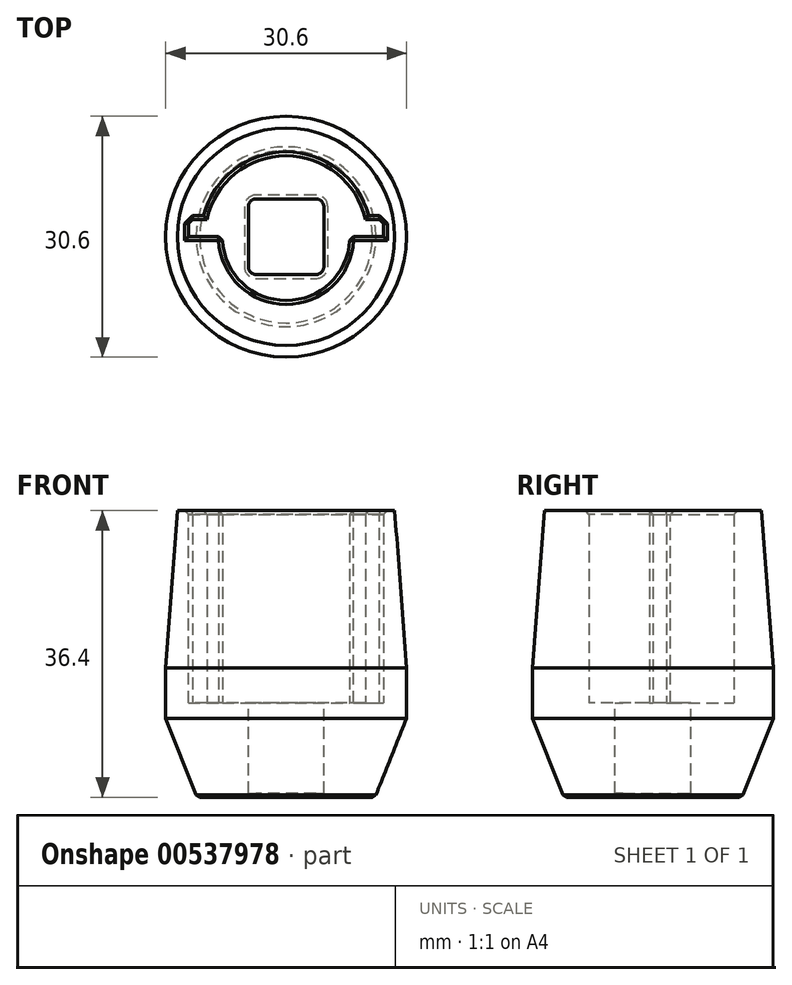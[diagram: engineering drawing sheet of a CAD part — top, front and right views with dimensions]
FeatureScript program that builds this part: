
annotation { "Feature Type Name" : "Feature", "Feature Type Description" : "" }
export const myFeature = defineFeature(function(context is Context, id is Id, definition is map)
    precondition{}
    {
        {
            var Q0;
            Q0=qCreatedBy(makeId("Top.planeOp"),FACE);
            var sketch = newSketch(context, id + "F0", { "sketchPlane" : qUnion([Q0])});
            skCircle(sketch, "E0", {"center": v(0, 0) * mm, "radius": 10.3 * mm});
            skCircle(sketch, "E1", {"center": v(0, 0) * mm, "radius": 15.3 * mm});
            skLineSegment(sketch, "E2", {"start": v(-15.3, 0) * mm, "end": v(15.3, 0) * mm});
            skCircle(sketch, "E3", {"center": v(0, 0) * mm, "radius": 8.1 * mm});
            skLineSegment(sketch, "E4.bottom", {"start": v(4.8, 4.8) * mm, "end": v(-4.8, 4.8) * mm});
            skLineSegment(sketch, "E4.top", {"start": v(4.8, -4.8) * mm, "end": v(-4.8, -4.8) * mm});
            skLineSegment(sketch, "E4.left", {"start": v(4.8, 4.8) * mm, "end": v(4.8, -4.8) * mm});
            skLineSegment(sketch, "E4.right", {"start": v(-4.8, 4.8) * mm, "end": v(-4.8, -4.8) * mm});
            skLineSegment(sketch, "E5", {"start": v(-10.06, 2.2) * mm, "end": v(-12.4, 2.2) * mm});
            skLineSegment(sketch, "E6", {"start": v(-12.4, 2.2) * mm, "end": v(-12.4, -2.2) * mm});
            skLineSegment(sketch, "E7", {"start": v(-12.4, -2.2) * mm, "end": v(-10.06, -2.2) * mm});
            skLineSegment(sketch, "E8.MirrorCS", {"start": v(10.06, 2.2) * mm, "end": v(12.4, 2.2) * mm});
            skLineSegment(sketch, "E9.MirrorCS", {"start": v(12.4, 2.2) * mm, "end": v(12.4, -2.2) * mm});
            skLineSegment(sketch, "E10.MirrorCS", {"start": v(12.4, -2.2) * mm, "end": v(10.06, -2.2) * mm});
            skSolve(sketch);
        }
        {
            var Q0;
            {var subQ5=sQuery(id+"F0.wireOp",EDGE,"E7");Q0=makeQuery(id+"F0.imprint","IMPRINT",FACE,{"disambiguationData":[TD([[makeQuery(id+"F0.imprint","IMPRINT",EDGE,{"derivedFrom":subQ5}),-1.0]])]});}
            var Q1;
            {var subQ9=sQuery(id+"F0.wireOp",EDGE,"E5");Q1=makeQuery(id+"F0.imprint","IMPRINT",FACE,{"disambiguationData":[TD([[makeQuery(id+"F0.imprint","IMPRINT",EDGE,{"derivedFrom":subQ9}),-1.0]])]});}
            extrude(context, id + "F1", {"entities" : qUnion([Q0, Q1]), "depth" : 24.4 * mm, "offsetDistance" : 25 * mm});
        }
        {
            var Q0;
            {var subQ0=sQuery(id+"F0.wireOp",EDGE,"E4.bottom");Q0=makeQuery(id+"F0.imprint","IMPRINT",FACE,{"disambiguationData":[TD([[makeQuery(id+"F0.imprint","IMPRINT",EDGE,{"derivedFrom":subQ0}),-1.0]])]});}
            var Q1;
            {var subQ0=sQuery(id+"F0.wireOp",EDGE,"E0");var subQ4=makeQuery(id+"F0.imprint","INTERSECT",VERTEX,{"derivedFrom":[subQ0,sQuery(id+"F0.wireOp",EDGE,"E8.MirrorCS")]});Q1=makeQuery(id+"F0.imprint","IMPRINT",FACE,{"disambiguationData":[TD([[makeQuery(id+"F0.imprint","IMPRINT",EDGE,{"disambiguationData":[TD([[subQ4,1.0]])],"derivedFrom":subQ0}),1.0]])]});}
            var Q2;
            {var subQ9=sQuery(id+"F0.wireOp",EDGE,"E5");Q2=makeQuery(id+"F0.imprint","IMPRINT",FACE,{"disambiguationData":[TD([[makeQuery(id+"F0.imprint","IMPRINT",EDGE,{"derivedFrom":subQ9}),-1.0]])]});}
            var Q3;
            {var subQ0=sQuery(id+"F0.wireOp",EDGE,"E4.top");Q3=makeQuery(id+"F0.imprint","IMPRINT",FACE,{"disambiguationData":[TD([[makeQuery(id+"F0.imprint","IMPRINT",EDGE,{"derivedFrom":subQ0}),1.0]])]});}
            var Q4;
            {var subQ1=sQuery(id+"F0.wireOp",EDGE,"E0");var subQ7=makeQuery(id+"F0.imprint","INTERSECT",VERTEX,{"derivedFrom":[subQ1,sQuery(id+"F0.wireOp",EDGE,"E7")]});Q4=makeQuery(id+"F0.imprint","IMPRINT",FACE,{"disambiguationData":[TD([[makeQuery(id+"F0.imprint","IMPRINT",EDGE,{"disambiguationData":[TD([[subQ7,1.0]])],"derivedFrom":subQ1}),1.0]])]});}
            var Q5;
            {var subQ5=sQuery(id+"F0.wireOp",EDGE,"E7");Q5=makeQuery(id+"F0.imprint","IMPRINT",FACE,{"disambiguationData":[TD([[makeQuery(id+"F0.imprint","IMPRINT",EDGE,{"derivedFrom":subQ5}),-1.0]])]});}
            var Q6;
            {var subQ0=sQuery(id+"F0.wireOp",EDGE,"E10.MirrorCS");Q6=makeQuery(id+"F0.imprint","IMPRINT",FACE,{"disambiguationData":[TD([[makeQuery(id+"F0.imprint","IMPRINT",EDGE,{"derivedFrom":subQ0}),-1.0]])]});}
            var Q7;
            {var subQ0=sQuery(id+"F0.wireOp",EDGE,"E8.MirrorCS");Q7=makeQuery(id+"F0.imprint","IMPRINT",FACE,{"disambiguationData":[TD([[makeQuery(id+"F0.imprint","IMPRINT",EDGE,{"derivedFrom":subQ0}),-1.0]])]});}
            var Q8;
            {var subQ0=sQuery(id+"F0.wireOp",EDGE,"E7");Q8=makeQuery(id+"F0.imprint","IMPRINT",FACE,{"disambiguationData":[TD([[makeQuery(id+"F0.imprint","IMPRINT",EDGE,{"derivedFrom":subQ0}),1.0]])]});}
            var Q9;
            {var subQ0=sQuery(id+"F0.wireOp",EDGE,"E5");Q9=makeQuery(id+"F0.imprint","IMPRINT",FACE,{"disambiguationData":[TD([[makeQuery(id+"F0.imprint","IMPRINT",EDGE,{"derivedFrom":subQ0}),1.0]])]});}
            extrude(context, id + "F2", {"entities" : qUnion([Q0, Q1, Q2, Q3, Q4, Q5, Q6, Q7, Q8, Q9]), "operationType" : NewBodyOperationType.ADD, "oppositeDirection" : true, "depth" : 12 * mm, "offsetDistance" : 25 * mm});
        }
        {
            var Q0;
            Q0=makeQuery(id+"F2.opExtrude","SWEPT_EDGE",EDGE,{"disambiguationData":[OSD([sQuery(id+"F0.wireOp",EDGE,"E4.bottom"),sQuery(id+"F0.wireOp",EDGE,"E4.right")])]});
            var Q1;
            Q1=makeQuery(id+"F2.opExtrude","SWEPT_EDGE",EDGE,{"disambiguationData":[OSD([sQuery(id+"F0.wireOp",EDGE,"E4.bottom"),sQuery(id+"F0.wireOp",EDGE,"E4.left")])]});
            var Q2;
            Q2=makeQuery(id+"F2.opExtrude","SWEPT_EDGE",EDGE,{"disambiguationData":[OSD([sQuery(id+"F0.wireOp",EDGE,"E4.top"),sQuery(id+"F0.wireOp",EDGE,"E4.left")])]});
            var Q3;
            Q3=makeQuery(id+"F2.opExtrude","SWEPT_EDGE",EDGE,{"disambiguationData":[OSD([sQuery(id+"F0.wireOp",EDGE,"E4.top"),sQuery(id+"F0.wireOp",EDGE,"E4.right")])]});
            fillet(context, id + "F3", {"entities" : qUnion([Q0, Q1, Q2, Q3]), "radius" : 1 * mm, "tangentPropagation" : true, "allowEdgeOverflow" : false});
        }
        {
            var Q0;
            {var subQ0=sQuery(id+"F0.wireOp",EDGE,"E10.MirrorCS");Q0=makeQuery(id+"F0.imprint","IMPRINT",FACE,{"disambiguationData":[TD([[makeQuery(id+"F0.imprint","IMPRINT",EDGE,{"derivedFrom":subQ0}),-1.0]])]});}
            var Q1;
            {var subQ1=sQuery(id+"F0.wireOp",EDGE,"E0");var subQ7=makeQuery(id+"F0.imprint","INTERSECT",VERTEX,{"derivedFrom":[subQ1,sQuery(id+"F0.wireOp",EDGE,"E7")]});Q1=makeQuery(id+"F0.imprint","IMPRINT",FACE,{"disambiguationData":[TD([[makeQuery(id+"F0.imprint","IMPRINT",EDGE,{"disambiguationData":[TD([[subQ7,1.0]])],"derivedFrom":subQ1}),1.0]])]});}
            var Q2;
            {var subQ0=sQuery(id+"F0.wireOp",EDGE,"E7");Q2=makeQuery(id+"F0.imprint","IMPRINT",FACE,{"disambiguationData":[TD([[makeQuery(id+"F0.imprint","IMPRINT",EDGE,{"derivedFrom":subQ0}),1.0]])]});}
            var Q3;
            Q3=makeQuery(id+"F1.opExtrude","CAP_FACE",FACE,{"disambiguationData":[OSD([sQuery(id+"F0.wireOp",EDGE,"E0"),sQuery(id+"F0.wireOp",EDGE,"E1"),sQuery(id+"F0.wireOp",EDGE,"E5"),sQuery(id+"F0.wireOp",EDGE,"E6"),sQuery(id+"F0.wireOp",EDGE,"E7"),sQuery(id+"F0.wireOp",EDGE,"E8.MirrorCS"),sQuery(id+"F0.wireOp",EDGE,"E9.MirrorCS"),sQuery(id+"F0.wireOp",EDGE,"E10.MirrorCS")])],"isStart":false});
            extrude(context, id + "F4", {"entities" : qUnion([Q0, Q1, Q2]), "operationType" : NewBodyOperationType.ADD, "endBound" : BoundingType.UP_TO_SURFACE, "depth" : 25 * mm, "endBoundEntityFace" : qUnion([Q3]), "offsetDistance" : 25 * mm});
        }
        {
            var Q0;
            Q0=makeQuery(id+"F2.opExtrude","CAP_EDGE",EDGE,{"disambiguationData":[OSD([sQuery(id+"F0.wireOp",EDGE,"E1")])],"isStart":false});
            chamfer(context, id + "F5", {"entities" : qUnion([Q0]), "chamferType" : ChamferType.TWO_OFFSETS, "width1" : 10 * mm, "oppositeDirection" : false, "width2" : 4 * mm, "tangentPropagation" : true});
        }
        {
            var Q0;
            Q0=makeQuery(id+"F1.opExtrude","CAP_EDGE",EDGE,{"disambiguationData":[OSD([sQuery(id+"F0.wireOp",EDGE,"E1")])],"isStart":false});
            chamfer(context, id + "F6", {"entities" : qUnion([Q0]), "chamferType" : ChamferType.TWO_OFFSETS, "width1" : 20 * mm, "oppositeDirection" : true, "width2" : 1.5 * mm, "tangentPropagation" : true});
        }
        {
            var Q0;
            Q0=makeQuery(id+"F2.opExtrude","CAP_FACE",FACE,{"disambiguationData":[OSD([sQuery(id+"F0.wireOp",EDGE,"E1"),sQuery(id+"F0.wireOp",EDGE,"E4.bottom"),sQuery(id+"F0.wireOp",EDGE,"E4.top"),sQuery(id+"F0.wireOp",EDGE,"E4.left"),sQuery(id+"F0.wireOp",EDGE,"E4.right")])],"isStart":false});
            var Q1;
            Q1=makeQuery(id+"F1.opExtrude","SWEPT_EDGE",EDGE,{"disambiguationData":[OSD([sQuery(id+"F0.wireOp",EDGE,"E8.MirrorCS"),sQuery(id+"F0.wireOp",EDGE,"E9.MirrorCS")])]});
            var Q2;
            Q2=makeQuery(id+"F1.opExtrude","SWEPT_EDGE",EDGE,{"disambiguationData":[OSD([sQuery(id+"F0.wireOp",EDGE,"E9.MirrorCS"),sQuery(id+"F0.wireOp",EDGE,"E10.MirrorCS")])]});
            var Q3;
            Q3=makeQuery(id+"F1.opExtrude","SWEPT_EDGE",EDGE,{"disambiguationData":[OSD([sQuery(id+"F0.wireOp",EDGE,"E5"),sQuery(id+"F0.wireOp",EDGE,"E6")])]});
            var Q4;
            Q4=makeQuery(id+"F1.opExtrude","SWEPT_EDGE",EDGE,{"disambiguationData":[OSD([sQuery(id+"F0.wireOp",EDGE,"E6"),sQuery(id+"F0.wireOp",EDGE,"E7")])]});
            var Q5;
            Q5=makeQuery(id+"F1.opExtrude","CAP_EDGE",EDGE,{"disambiguationData":[OSD([sQuery(id+"F0.wireOp",EDGE,"E7")])],"isStart":false});
            var Q6;
            Q6=makeQuery(id+"F1.opExtrude","CAP_EDGE",EDGE,{"disambiguationData":[OSD([sQuery(id+"F0.wireOp",EDGE,"E10.MirrorCS")])],"isStart":false});
            var Q7;
            {var subQ0=sQuery(id+"F0.wireOp",EDGE,"E0");Q7=makeQuery(id+"F1.opExtrude","CAP_EDGE",EDGE,{"disambiguationData":[OSD([subQ0]),TDD([makeQuery(id+"F0.imprint","IMPRINT",EDGE,{"disambiguationData":[TD([[makeQuery(id+"F0.imprint","INTERSECT",VERTEX,{"derivedFrom":[subQ0,sQuery(id+"F0.wireOp",EDGE,"E5")]}),1.0]])],"derivedFrom":subQ0})])],"isStart":true});}
            var Q8;
            {var subQ0=sQuery(id+"F0.wireOp",EDGE,"E0");Q8=makeQuery(id+"F1.opExtrude","CAP_EDGE",EDGE,{"disambiguationData":[OSD([subQ0]),TDD([makeQuery(id+"F0.imprint","IMPRINT",EDGE,{"disambiguationData":[TD([[makeQuery(id+"F0.imprint","INTERSECT",VERTEX,{"derivedFrom":[subQ0,sQuery(id+"F0.wireOp",EDGE,"E7")]}),-1.0]])],"derivedFrom":subQ0})])],"isStart":true});}
            var Q9;
            {var subQ0=sQuery(id+"F0.wireOp",EDGE,"E0");Q9=makeQuery(id+"F1.opExtrude","CAP_EDGE",EDGE,{"disambiguationData":[OSD([subQ0]),TDD([makeQuery(id+"F0.imprint","IMPRINT",EDGE,{"disambiguationData":[TD([[makeQuery(id+"F0.imprint","INTERSECT",VERTEX,{"derivedFrom":[subQ0,sQuery(id+"F0.wireOp",EDGE,"E5")]}),1.0]])],"derivedFrom":subQ0})])],"isStart":false});}
            var Q10;
            {var subQ0=sQuery(id+"F0.wireOp",EDGE,"E0");Q10=makeQuery(id+"F1.opExtrude","CAP_EDGE",EDGE,{"disambiguationData":[OSD([subQ0]),TDD([makeQuery(id+"F0.imprint","IMPRINT",EDGE,{"disambiguationData":[TD([[makeQuery(id+"F0.imprint","INTERSECT",VERTEX,{"derivedFrom":[subQ0,sQuery(id+"F0.wireOp",EDGE,"E7")]}),-1.0]])],"derivedFrom":subQ0})])],"isStart":false});}
            var Q11;
            {var subQ0=sQuery(id+"F0.wireOp",EDGE,"E3");var subQ1=sQuery(id+"F0.wireOp",EDGE,"E2");Q11=makeQuery(id+"F4.opExtrude","SWEPT_EDGE",EDGE,{"disambiguationData":[OSD([subQ1,subQ0]),TDD([makeQuery(id+"F0.imprint","INTERSECT",VERTEX,{"disambiguationData":[OD(1.0)],"derivedFrom":[subQ1,subQ0]})])]});}
            var Q12;
            {var subQ0=sQuery(id+"F0.wireOp",EDGE,"E3");var subQ1=sQuery(id+"F0.wireOp",EDGE,"E2");Q12=makeQuery(id+"F4.opExtrude","SWEPT_EDGE",EDGE,{"disambiguationData":[OSD([subQ1,subQ0]),TDD([makeQuery(id+"F0.imprint","INTERSECT",VERTEX,{"disambiguationData":[OD(0.0)],"derivedFrom":[subQ1,subQ0]})])]});}
            var Q13;
            Q13=makeQuery(id+"F4.opExtrude","CAP_EDGE",EDGE,{"disambiguationData":[OSD([sQuery(id+"F0.wireOp",EDGE,"E3")])],"isStart":false});
            var Q14;
            {var subQ0=sQuery(id+"F0.wireOp",EDGE,"E2");var subQ1=makeQuery(id+"F0.imprint","INTERSECT",VERTEX,{"disambiguationData":[OD(0.0)],"derivedFrom":[sQuery(id+"F0.wireOp",EDGE,"E0"),subQ0]});Q14=makeQuery(id+"F4.opExtrude","CAP_EDGE",EDGE,{"disambiguationData":[OSD([subQ0]),TDD([makeQuery(id+"F0.imprint","IMPRINT",EDGE,{"disambiguationData":[TD([[subQ1,1.0]])],"derivedFrom":subQ0}),makeQuery(id+"F0.imprint","IMPRINT",EDGE,{"disambiguationData":[TD([[subQ1,-1.0]])],"derivedFrom":subQ0})])],"isStart":false});}
            var Q15;
            {var subQ0=sQuery(id+"F0.wireOp",EDGE,"E2");var subQ1=makeQuery(id+"F0.imprint","INTERSECT",VERTEX,{"disambiguationData":[OD(1.0)],"derivedFrom":[sQuery(id+"F0.wireOp",EDGE,"E0"),subQ0]});Q15=makeQuery(id+"F4.opExtrude","CAP_EDGE",EDGE,{"disambiguationData":[OSD([subQ0]),TDD([makeQuery(id+"F0.imprint","IMPRINT",EDGE,{"disambiguationData":[TD([[subQ1,1.0]])],"derivedFrom":subQ0}),makeQuery(id+"F0.imprint","IMPRINT",EDGE,{"disambiguationData":[TD([[subQ1,-1.0]])],"derivedFrom":subQ0})])],"isStart":false});}
            var Q16;
            Q16=makeQuery(id+"F1.opExtrude","CAP_EDGE",EDGE,{"disambiguationData":[OSD([sQuery(id+"F0.wireOp",EDGE,"E5")])],"isStart":false});
            var Q17;
            Q17=makeQuery(id+"F1.opExtrude","CAP_EDGE",EDGE,{"disambiguationData":[OSD([sQuery(id+"F0.wireOp",EDGE,"E8.MirrorCS")])],"isStart":false});
            chamfer(context, id + "F7", {"entities" : qUnion([Q0, Q1, Q2, Q3, Q4, Q5, Q6, Q7, Q8, Q9, Q10, Q11, Q12, Q13, Q14, Q15, Q16, Q17]), "width" : .5 * mm, "tangentPropagation" : true});
        }
    });
